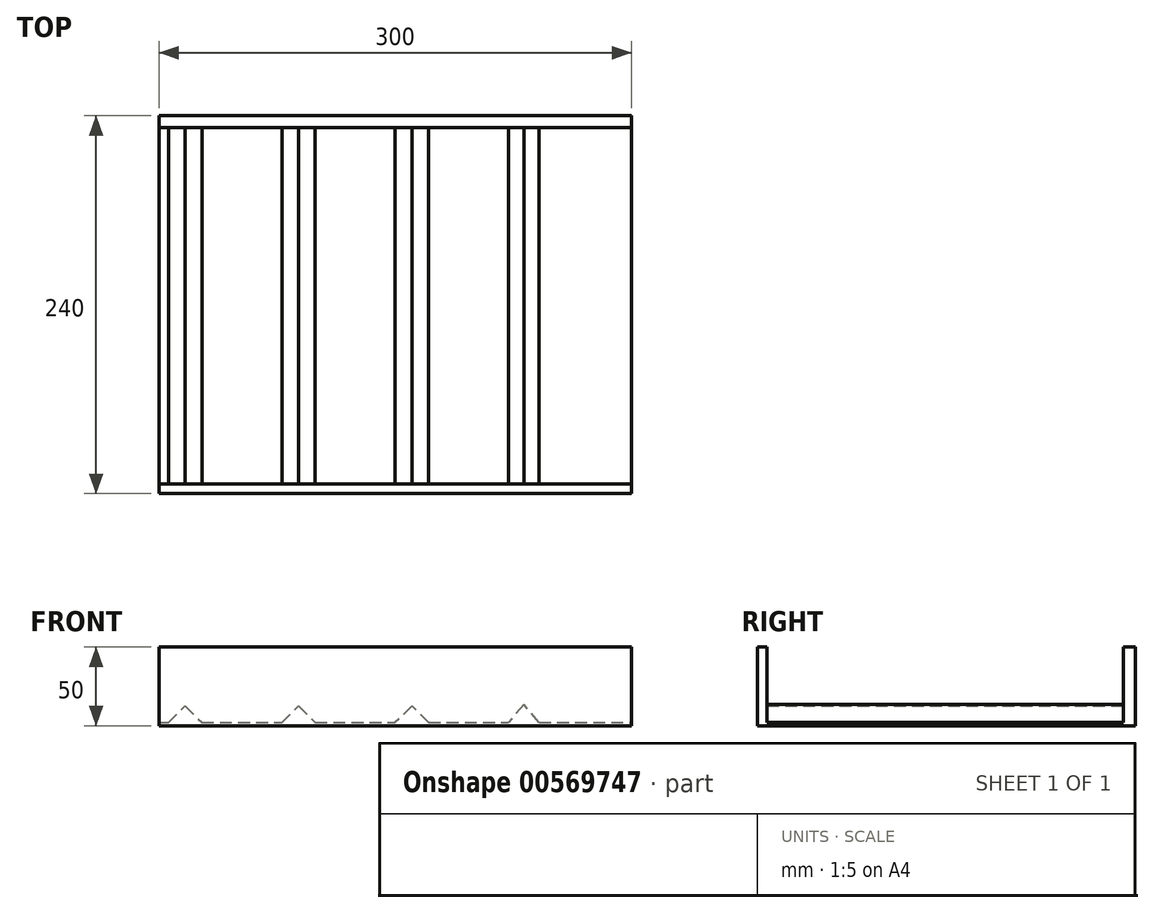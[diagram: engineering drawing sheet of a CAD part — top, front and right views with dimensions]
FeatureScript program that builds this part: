
annotation { "Feature Type Name" : "Feature", "Feature Type Description" : "" }
export const myFeature = defineFeature(function(context is Context, id is Id, definition is map)
    precondition{}
    {
        {
            var Q0;
            Q0=qCreatedBy(makeId("Top.planeOp"),FACE);
            var sketch = newSketch(context, id + "F0", { "sketchPlane" : qUnion([Q0])});
            skLineSegment(sketch, "E0.bottom", {"start": v(-135.25, 189.4) * mm, "end": v(164.75, 189.4) * mm});
            skLineSegment(sketch, "E0.top", {"start": v(-135.25, -50.6) * mm, "end": v(164.75, -50.6) * mm});
            skLineSegment(sketch, "E0.left", {"start": v(-135.25, 189.4) * mm, "end": v(-135.25, -50.6) * mm});
            skLineSegment(sketch, "E0.right", {"start": v(164.75, 189.4) * mm, "end": v(164.75, -50.6) * mm});
            skSolve(sketch);
        }
        {
            var Q0;
            Q0=makeQuery(id+"F0.imprint","IMPRINT",FACE,{"disambiguationData":[TD([[makeQuery(id+"F0.imprint","IMPRINT",EDGE,{"derivedFrom":sQuery(id+"F0.wireOp",EDGE,"E0.bottom")}),-1.0]])]});
            extrude(context, id + "F1", {"entities" : qUnion([Q0]), "depth" : 50 * mm, "offsetDistance" : 25 * mm});
        }
        {
            var Q0;
            Q0=makeQuery(id+"F1.opExtrude","CAP_FACE",FACE,{"disambiguationData":[OSD([sQuery(id+"F0.wireOp",EDGE,"E0.bottom"),sQuery(id+"F0.wireOp",EDGE,"E0.top"),sQuery(id+"F0.wireOp",EDGE,"E0.left"),sQuery(id+"F0.wireOp",EDGE,"E0.right")])],"isStart":false});
            var sketch = newSketch(context, id + "F2", { "sketchPlane" : qUnion([Q0])});
            skLineSegment(sketch, "E1.bottom", {"start": v(-135.25, -44.41) * mm, "end": v(164.75, -44.41) * mm});
            skLineSegment(sketch, "E1.top", {"start": v(-135.25, 181.77) * mm, "end": v(164.75, 181.77) * mm});
            skLineSegment(sketch, "E1.left", {"start": v(-135.25, -44.41) * mm, "end": v(-135.25, 181.77) * mm});
            skLineSegment(sketch, "E1.right", {"start": v(164.75, -44.41) * mm, "end": v(164.75, 181.77) * mm});
            skSolve(sketch);
        }
        {
            var Q0;
            Q0=makeQuery(id+"F2.imprint","IMPRINT",FACE,{"disambiguationData":[TD([[makeQuery(id+"F2.imprint","IMPRINT",EDGE,{"derivedFrom":sQuery(id+"F2.wireOp",EDGE,"E1.bottom")}),1.0]])]});
            extrude(context, id + "F3", {"entities" : qUnion([Q0]), "operationType" : NewBodyOperationType.REMOVE, "oppositeDirection" : true, "depth" : 48 * mm, "offsetDistance" : 25 * mm});
        }
        {
            var Q0;
            Q0=makeQuery(id+"F3.boolean.opBoolean","COPY",FACE,{"derivedFrom":makeQuery(id+"F3.opExtrude","SWEPT_FACE",FACE,{"disambiguationData":[OSD([sQuery(id+"F2.wireOp",EDGE,"E1.top")])]})});
            var sketch = newSketch(context, id + "F4", { "sketchPlane" : qUnion([Q0])});
            skLineSegment(sketch, "E2", {"start": v(106, 2) * mm, "end": v(96.38, 13.5) * mm});
            skLineSegment(sketch, "E3", {"start": v(96.38, 13.5) * mm, "end": v(86.76, 2) * mm});
            skLineSegment(sketch, "E4", {"start": v(86.76, 2) * mm, "end": v(106, 2) * mm});
            skLineSegment(sketch, "E5", {"start": v(-129.3, 2) * mm, "end": v(-118.7, 12.6) * mm});
            skLineSegment(sketch, "E6", {"start": v(-118.7, 12.6) * mm, "end": v(-108.08, 2) * mm});
            skLineSegment(sketch, "E7", {"start": v(-129.3, 2) * mm, "end": v(-108.08, 2) * mm});
            skLineSegment(sketch, "E8", {"start": v(35.96, 2) * mm, "end": v(25.35, 12.6) * mm});
            skLineSegment(sketch, "E9", {"start": v(25.35, 12.6) * mm, "end": v(14.75, 2) * mm});
            skLineSegment(sketch, "E10", {"start": v(14.75, 2) * mm, "end": v(35.96, 2) * mm});
            skLineSegment(sketch, "E11", {"start": v(-57.28, 2) * mm, "end": v(-46.67, 12.6) * mm});
            skLineSegment(sketch, "E12", {"start": v(-46.67, 12.6) * mm, "end": v(-36.05, 2) * mm});
            skLineSegment(sketch, "E13", {"start": v(-57.28, 2) * mm, "end": v(-36.05, 2) * mm});
            skSolve(sketch);
        }
        {
            var Q0;
            Q0=makeQuery(id+"F4.imprint","IMPRINT",FACE,{"disambiguationData":[TD([[makeQuery(id+"F4.imprint","IMPRINT",EDGE,{"derivedFrom":sQuery(id+"F4.wireOp",EDGE,"E5")}),-1.0]])]});
            var Q1;
            Q1=makeQuery(id+"F4.imprint","IMPRINT",FACE,{"disambiguationData":[TD([[makeQuery(id+"F4.imprint","IMPRINT",EDGE,{"derivedFrom":sQuery(id+"F4.wireOp",EDGE,"E8")}),1.0]])]});
            var Q2;
            Q2=makeQuery(id+"F4.imprint","IMPRINT",FACE,{"disambiguationData":[TD([[makeQuery(id+"F4.imprint","IMPRINT",EDGE,{"derivedFrom":sQuery(id+"F4.wireOp",EDGE,"E2")}),1.0]])]});
            var Q3;
            Q3=makeQuery(id+"F4.imprint","IMPRINT",FACE,{"disambiguationData":[TD([[makeQuery(id+"F4.imprint","IMPRINT",EDGE,{"derivedFrom":sQuery(id+"F4.wireOp",EDGE,"E11")}),-1.0]])]});
            extrude(context, id + "F5", {"entities" : qUnion([Q0, Q1, Q2, Q3]), "operationType" : NewBodyOperationType.ADD, "depth" : 228.9 * mm, "offsetDistance" : 25 * mm});
        }
    });
